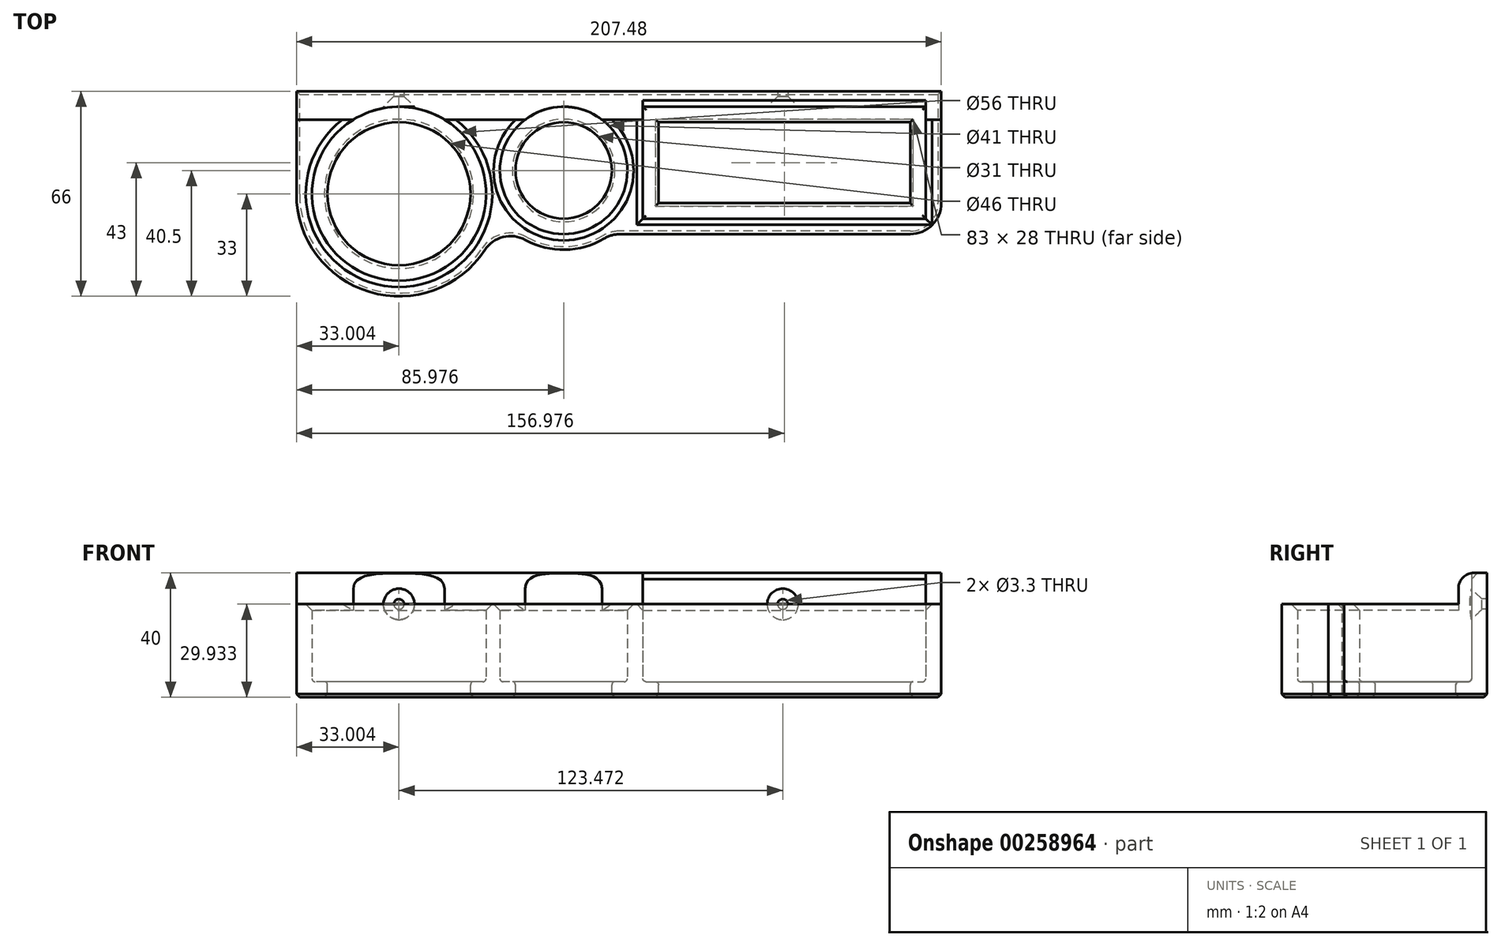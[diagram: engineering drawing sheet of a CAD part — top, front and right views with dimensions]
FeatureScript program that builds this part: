
annotation { "Feature Type Name" : "Feature", "Feature Type Description" : "" }
export const myFeature = defineFeature(function(context is Context, id is Id, definition is map)
    precondition{}
    {
        {
            var Q0;
            Q0=qCreatedBy(makeId("Top.planeOp"),FACE);
            var sketch = newSketch(context, id + "F0", { "sketchPlane" : qUnion([Q0])});
            skCircle(sketch, "E0", {"center": v(-34.24, -28) * mm, "radius": 28 * mm});
            skCircle(sketch, "E1", {"center": v(18.74, -20.5) * mm, "radius": 20.5 * mm});
            skLineSegment(sketch, "E2.bottom", {"start": v(44.24, 0) * mm, "end": v(135.24, 0) * mm});
            skLineSegment(sketch, "E2.top", {"start": v(44.24, -36) * mm, "end": v(135.24, -36) * mm});
            skLineSegment(sketch, "E2.left", {"start": v(44.24, 0) * mm, "end": v(44.24, -36) * mm});
            skLineSegment(sketch, "E2.right", {"start": v(135.24, 0) * mm, "end": v(135.24, -36) * mm});
            skCircle(sketch, "E3.0", {"center": v(-34.24, -28) * mm, "radius": 33 * mm, "construction": true});
            skCircle(sketch, "E4.0", {"center": v(18.74, -20.5) * mm, "radius": 25.5 * mm, "construction": true});
            skLineSegment(sketch, "E5", {"start": v(-67.24, -28) * mm, "end": v(-67.24, 5) * mm});
            skLineSegment(sketch, "E6", {"start": v(-67.24, 5) * mm, "end": v(140.24, 5) * mm});
            skLineSegment(sketch, "E7", {"start": v(140.24, 5) * mm, "end": v(140.24, -41) * mm});
            skLineSegment(sketch, "E8", {"start": v(140.24, -41) * mm, "end": v(33.9, -41) * mm});
            skArc(sketch, "E9", {"start": v(-67.24, -28) * mm, "mid": v(-37.9, -60.8) * mm, "end": v(-2.05, -35.27) * mm});
            skArc(sketch, "E10", {"start": v(-2.05, -35.27) * mm, "mid": v(14.73, -45.68) * mm, "end": v(33.9, -41) * mm});
            skSolve(sketch);
        }
        {
            var Q0;
            Q0=makeQuery(id+"F0.imprint","IMPRINT",FACE,{"disambiguationData":[TD([[makeQuery(id+"F0.imprint","IMPRINT",EDGE,{"derivedFrom":sQuery(id+"F0.wireOp",EDGE,"E0")}),-1.0]])]});
            extrude(context, id + "F1", {"entities" : qUnion([Q0]), "depth" : 30 * mm});
        }
        {
            var Q0;
            Q0=makeQuery(id+"F0.imprint","IMPRINT",FACE,{"disambiguationData":[TD([[makeQuery(id+"F0.imprint","IMPRINT",EDGE,{"derivedFrom":sQuery(id+"F0.wireOp",EDGE,"E0")}),1.0]])]});
            var Q1;
            Q1=makeQuery(id+"F0.imprint","IMPRINT",FACE,{"disambiguationData":[TD([[makeQuery(id+"F0.imprint","IMPRINT",EDGE,{"derivedFrom":sQuery(id+"F0.wireOp",EDGE,"E1")}),1.0]])]});
            var Q2;
            Q2=makeQuery(id+"F0.imprint","IMPRINT",FACE,{"disambiguationData":[TD([[makeQuery(id+"F0.imprint","IMPRINT",EDGE,{"derivedFrom":sQuery(id+"F0.wireOp",EDGE,"E2.bottom")}),-1.0]])]});
            extrude(context, id + "F2", {"entities" : qUnion([Q0, Q1, Q2]), "operationType" : NewBodyOperationType.ADD, "depth" : 5 * mm});
        }
        {
            var Q0;
            Q0=makeQuery(id+"F1.opExtrude","CAP_FACE",FACE,{"disambiguationData":[OSD([sQuery(id+"F0.wireOp",EDGE,"E0"),sQuery(id+"F0.wireOp",EDGE,"E1"),sQuery(id+"F0.wireOp",EDGE,"E2.bottom"),sQuery(id+"F0.wireOp",EDGE,"E2.top"),sQuery(id+"F0.wireOp",EDGE,"E2.left"),sQuery(id+"F0.wireOp",EDGE,"E2.right"),sQuery(id+"F0.wireOp",EDGE,"E5"),sQuery(id+"F0.wireOp",EDGE,"E6"),sQuery(id+"F0.wireOp",EDGE,"E7"),sQuery(id+"F0.wireOp",EDGE,"E8"),sQuery(id+"F0.wireOp",EDGE,"E9"),sQuery(id+"F0.wireOp",EDGE,"E10")])],"isStart":false});
            var sketch = newSketch(context, id + "F3", { "sketchPlane" : qUnion([Q0])});
            skLineSegment(sketch, "E11.bottom", {"start": v(-70.35, 8.83) * mm, "end": v(146.1, 8.83) * mm});
            skLineSegment(sketch, "E11.top", {"start": v(-70.35, -4.18) * mm, "end": v(146.1, -4.18) * mm});
            skLineSegment(sketch, "E11.left", {"start": v(-70.35, 8.83) * mm, "end": v(-70.35, -4.18) * mm});
            skLineSegment(sketch, "E11.right", {"start": v(146.1, 8.83) * mm, "end": v(146.1, -4.18) * mm});
            skSolve(sketch);
        }
        {
            var Q0;
            {var subQ5=makeQuery(id+"F1.opExtrude","CAP_EDGE",EDGE,{"disambiguationData":[OSD([sQuery(id+"F0.wireOp",EDGE,"E2.bottom")])],"isStart":false});Q0=makeQuery(id+"F3.imprint","IMPRINT",FACE,{"disambiguationData":[TD([[makeQuery(id+"F3.imprint","IMPRINT",EDGE,{"derivedFrom":subQ5}),1.0]])]});}
            extrude(context, id + "F4", {"entities" : qUnion([Q0]), "operationType" : NewBodyOperationType.ADD, "depth" : 10 * mm});
        }
        {
            var Q0;
            {var subQ0=sQuery(id+"F3.wireOp",EDGE,"E11.top");Q0=makeQuery(id+"F4.opExtrude","CAP_EDGE",EDGE,{"disambiguationData":[OSD([subQ0]),TDD([makeQuery(id+"F3.imprint","IMPRINT",EDGE,{"disambiguationData":[TD([[makeQuery(id+"F3.imprint","INTERSECT",VERTEX,{"derivedFrom":[makeQuery(id+"F1.opExtrude","CAP_EDGE",EDGE,{"disambiguationData":[OSD([sQuery(id+"F0.wireOp",EDGE,"E5")])],"isStart":false}),subQ0]}),-1.0]])],"derivedFrom":subQ0})])],"isStart":false});}
            var Q1;
            {var subQ0=sQuery(id+"F3.wireOp",EDGE,"E11.top");Q1=makeQuery(id+"F4.opExtrude","CAP_EDGE",EDGE,{"disambiguationData":[OSD([subQ0]),TDD([makeQuery(id+"F3.imprint","IMPRINT",EDGE,{"disambiguationData":[TD([[makeQuery(id+"F3.imprint","INTERSECT",VERTEX,{"disambiguationData":[OD(1.0)],"derivedFrom":[makeQuery(id+"F1.opExtrude","CAP_EDGE",EDGE,{"disambiguationData":[OSD([sQuery(id+"F0.wireOp",EDGE,"E0")])],"isStart":false}),subQ0]}),-1.0]])],"derivedFrom":subQ0})])],"isStart":false});}
            var Q2;
            {var subQ0=sQuery(id+"F3.wireOp",EDGE,"E11.top");Q2=makeQuery(id+"F4.opExtrude","CAP_EDGE",EDGE,{"disambiguationData":[OSD([subQ0]),TDD([makeQuery(id+"F3.imprint","IMPRINT",EDGE,{"disambiguationData":[TD([[makeQuery(id+"F3.imprint","INTERSECT",VERTEX,{"disambiguationData":[OD(1.0)],"derivedFrom":[makeQuery(id+"F1.opExtrude","CAP_EDGE",EDGE,{"disambiguationData":[OSD([sQuery(id+"F0.wireOp",EDGE,"E1")])],"isStart":false}),subQ0]}),-1.0]])],"derivedFrom":subQ0})])],"isStart":false});}
            var Q3;
            {var subQ0=sQuery(id+"F3.wireOp",EDGE,"E11.top");Q3=makeQuery(id+"F4.opExtrude","CAP_EDGE",EDGE,{"disambiguationData":[OSD([subQ0]),TDD([makeQuery(id+"F3.imprint","IMPRINT",EDGE,{"disambiguationData":[TD([[makeQuery(id+"F3.imprint","INTERSECT",VERTEX,{"disambiguationData":[OD(1.0)],"derivedFrom":[makeQuery(id+"F1.opExtrude","CAP_EDGE",EDGE,{"disambiguationData":[OSD([sQuery(id+"F0.wireOp",EDGE,"E1")])],"isStart":false}),subQ0]}),-1.0]])],"derivedFrom":subQ0})])],"isStart":true});}
            var Q4;
            {var subQ0=sQuery(id+"F3.wireOp",EDGE,"E11.top");Q4=makeQuery(id+"F4.opExtrude","CAP_EDGE",EDGE,{"disambiguationData":[OSD([subQ0]),TDD([makeQuery(id+"F3.imprint","IMPRINT",EDGE,{"disambiguationData":[TD([[makeQuery(id+"F3.imprint","INTERSECT",VERTEX,{"disambiguationData":[OD(1.0)],"derivedFrom":[makeQuery(id+"F1.opExtrude","CAP_EDGE",EDGE,{"disambiguationData":[OSD([sQuery(id+"F0.wireOp",EDGE,"E0")])],"isStart":false}),subQ0]}),-1.0]])],"derivedFrom":subQ0})])],"isStart":true});}
            var Q5;
            {var subQ0=sQuery(id+"F3.wireOp",EDGE,"E11.top");Q5=makeQuery(id+"F4.opExtrude","CAP_EDGE",EDGE,{"disambiguationData":[OSD([subQ0]),TDD([makeQuery(id+"F3.imprint","IMPRINT",EDGE,{"disambiguationData":[TD([[makeQuery(id+"F3.imprint","INTERSECT",VERTEX,{"derivedFrom":[makeQuery(id+"F1.opExtrude","CAP_EDGE",EDGE,{"disambiguationData":[OSD([sQuery(id+"F0.wireOp",EDGE,"E5")])],"isStart":false}),subQ0]}),-1.0]])],"derivedFrom":subQ0})])],"isStart":true});}
            var Q6;
            {var subQ0=sQuery(id+"F3.wireOp",EDGE,"E11.top");Q6=makeQuery(id+"F4.opExtrude","CAP_EDGE",EDGE,{"disambiguationData":[OSD([subQ0]),TDD([makeQuery(id+"F3.imprint","IMPRINT",EDGE,{"disambiguationData":[TD([[makeQuery(id+"F3.imprint","INTERSECT",VERTEX,{"derivedFrom":[makeQuery(id+"F1.opExtrude","CAP_EDGE",EDGE,{"disambiguationData":[OSD([sQuery(id+"F0.wireOp",EDGE,"E7")])],"isStart":false}),subQ0]}),1.0]])],"derivedFrom":subQ0})])],"isStart":true});}
            var Q7;
            {var subQ0=sQuery(id+"F3.wireOp",EDGE,"E11.top");Q7=makeQuery(id+"F4.opExtrude","CAP_EDGE",EDGE,{"disambiguationData":[OSD([subQ0]),TDD([makeQuery(id+"F3.imprint","IMPRINT",EDGE,{"disambiguationData":[TD([[makeQuery(id+"F3.imprint","INTERSECT",VERTEX,{"derivedFrom":[makeQuery(id+"F1.opExtrude","CAP_EDGE",EDGE,{"disambiguationData":[OSD([sQuery(id+"F0.wireOp",EDGE,"E7")])],"isStart":false}),subQ0]}),1.0]])],"derivedFrom":subQ0})])],"isStart":false});}
            fillet(context, id + "F5", {"entities" : qUnion([Q0, Q1, Q2, Q3, Q4, Q5, Q6, Q7]), "radius" : 5 * mm, "tangentPropagation" : true, "allowEdgeOverflow" : false});
        }
        {
            var Q0;
            Q0=qCreatedBy(makeId("Front.planeOp"),FACE);
            cPlane(context, id + "F6", {"entities" : qUnion([Q0]), "cplaneType" : CPlaneType.OFFSET, "offset" : 1 * mm, "width" : 150 * mm, "height" : 150 * mm});
        }
        {
            var Q0;
            Q0=qCreatedBy(id+"F6.planeOp",FACE);
            var sketch = newSketch(context, id + "F7", { "sketchPlane" : qUnion([Q0])});
            skPoint(sketch, "E12", {"position": v(-34.24, 29.93) * mm});
            skPoint(sketch, "E13", {"position": v(89.24, 29.93) * mm});
            skSolve(sketch);
        }
        {
            var Q0;
            Q0=sQuery(id+"F7.wireOp",VERTEX,"E13");
            var Q1;
            Q1=sQuery(id+"F7.wireOp",VERTEX,"E12");
            var Q2;
            Q2=makeQuery(id+"F1.opExtrude","SWEPT_BODY",BODY,{"disambiguationData":[OSD([sQuery(id+"F0.wireOp",EDGE,"E0"),sQuery(id+"F0.wireOp",EDGE,"E1"),sQuery(id+"F0.wireOp",EDGE,"E2.bottom"),sQuery(id+"F0.wireOp",EDGE,"E2.top"),sQuery(id+"F0.wireOp",EDGE,"E2.left"),sQuery(id+"F0.wireOp",EDGE,"E2.right"),sQuery(id+"F0.wireOp",EDGE,"E5"),sQuery(id+"F0.wireOp",EDGE,"E6"),sQuery(id+"F0.wireOp",EDGE,"E7"),sQuery(id+"F0.wireOp",EDGE,"E8"),sQuery(id+"F0.wireOp",EDGE,"E9"),sQuery(id+"F0.wireOp",EDGE,"E10")])]});
            hole(context, id + "F8", {"style" : HoleStyle.C_SINK, "endStyle" : HoleEndStyle.BLIND, "holeDiameter" : 3.3 * mm, "cSinkDiameter" : 10 * mm, "cSinkAngle" : 90 * degree, "holeDepth" : 10 * mm, "tappedDepth" : 7 * mm, "tapClearance" : 0, "locations" : qUnion([Q0, Q1]), "scope" : qUnion([Q2])});
        }
        {
            var Q0;
            Q0=makeQuery(id+"F1.opExtrude","SWEPT_EDGE",EDGE,{"disambiguationData":[OSD([sQuery(id+"F0.wireOp",EDGE,"E9"),sQuery(id+"F0.wireOp",EDGE,"E10")])]});
            var Q1;
            Q1=makeQuery(id+"F1.opExtrude","SWEPT_EDGE",EDGE,{"disambiguationData":[OSD([sQuery(id+"F0.wireOp",EDGE,"E8"),sQuery(id+"F0.wireOp",EDGE,"E10")])]});
            var Q2;
            Q2=makeQuery(id+"F1.opExtrude","SWEPT_EDGE",EDGE,{"disambiguationData":[OSD([sQuery(id+"F0.wireOp",EDGE,"E7"),sQuery(id+"F0.wireOp",EDGE,"E8")])]});
            fillet(context, id + "F9", {"entities" : qUnion([Q0, Q1, Q2]), "radius" : 10 * mm, "tangentPropagation" : true, "allowEdgeOverflow" : false});
        }
        {
            var Q0;
            Q0=makeQuery(id+"F1.opExtrude","CAP_EDGE",EDGE,{"disambiguationData":[OSD([sQuery(id+"F0.wireOp",EDGE,"E0")])],"isStart":false});
            var Q1;
            Q1=makeQuery(id+"F1.opExtrude","CAP_EDGE",EDGE,{"disambiguationData":[OSD([sQuery(id+"F0.wireOp",EDGE,"E1")])],"isStart":false});
            var Q2;
            Q2=makeQuery(id+"F1.opExtrude","CAP_EDGE",EDGE,{"disambiguationData":[OSD([sQuery(id+"F0.wireOp",EDGE,"E2.left")])],"isStart":false});
            var Q3;
            Q3=makeQuery(id+"F1.opExtrude","CAP_EDGE",EDGE,{"disambiguationData":[OSD([sQuery(id+"F0.wireOp",EDGE,"E2.top")])],"isStart":false});
            var Q4;
            Q4=makeQuery(id+"F1.opExtrude","CAP_EDGE",EDGE,{"disambiguationData":[OSD([sQuery(id+"F0.wireOp",EDGE,"E2.right")])],"isStart":false});
            var Q5;
            {var subQ0=sQuery(id+"F0.wireOp",EDGE,"E2.bottom");var subQ1=sQuery(id+"F3.wireOp",EDGE,"E11.top");Q5=makeQuery(id+"F5.opFillet","BLEND_EDGE",EDGE,{"blendedFrom":[makeQuery(id+"F4.opExtrude","CAP_EDGE",EDGE,{"disambiguationData":[OSD([subQ1]),TDD([makeQuery(id+"F3.imprint","IMPRINT",EDGE,{"disambiguationData":[TD([[makeQuery(id+"F3.imprint","INTERSECT",VERTEX,{"derivedFrom":[makeQuery(id+"F1.opExtrude","CAP_EDGE",EDGE,{"disambiguationData":[OSD([sQuery(id+"F0.wireOp",EDGE,"E5")])],"isStart":false}),subQ1]}),-1.0]])],"derivedFrom":subQ1})])],"isStart":false}),makeQuery(id+"F4.boolean.opBoolean","MERGE",FACE,{"derivedFrom":[makeQuery(id+"F1.opExtrude","SWEPT_FACE",FACE,{"disambiguationData":[OSD([subQ0])]}),makeQuery(id+"F4.opExtrude","SWEPT_FACE",FACE,{"disambiguationData":[OSD([subQ0])]})]})],"blendedInto":[makeQuery(id+"F4.boolean.opBoolean","MERGE",FACE,{"derivedFrom":[makeQuery(id+"F1.opExtrude","SWEPT_FACE",FACE,{"disambiguationData":[OSD([subQ0])]}),makeQuery(id+"F4.opExtrude","SWEPT_FACE",FACE,{"disambiguationData":[OSD([subQ0])]})]})]});}
            chamfer(context, id + "F10", {"entities" : qUnion([Q0, Q1, Q2, Q3, Q4, Q5]), "width" : 2 * mm, "tangentPropagation" : true});
        }
        {
            var Q0;
            Q0=makeQuery(id+"F2.opExtrude","CAP_FACE",FACE,{"disambiguationData":[OSD([sQuery(id+"F0.wireOp",EDGE,"E0")])],"isStart":false});
            var sketch = newSketch(context, id + "F11", { "sketchPlane" : qUnion([Q0])});
            skCircle(sketch, "E14", {"center": v(-34.24, -28) * mm, "radius": 23 * mm});
            skCircle(sketch, "E15", {"center": v(18.74, -20.5) * mm, "radius": 15.5 * mm});
            skLineSegment(sketch, "E16.0", {"start": v(49.24, -5) * mm, "end": v(49.24, -31) * mm});
            skLineSegment(sketch, "E16.1", {"start": v(49.24, -5) * mm, "end": v(130.24, -5) * mm});
            skLineSegment(sketch, "E16.2", {"start": v(130.24, -5) * mm, "end": v(130.24, -31) * mm});
            skLineSegment(sketch, "E16.3", {"start": v(49.24, -31) * mm, "end": v(130.24, -31) * mm});
            skSolve(sketch);
        }
        {
            var Q0;
            Q0=makeQuery(id+"F11.imprint","IMPRINT",FACE,{"disambiguationData":[TD([[makeQuery(id+"F11.imprint","IMPRINT",EDGE,{"derivedFrom":sQuery(id+"F11.wireOp",EDGE,"E14")}),1.0]])]});
            var Q1;
            Q1=makeQuery(id+"F11.imprint","IMPRINT",FACE,{"disambiguationData":[TD([[makeQuery(id+"F11.imprint","IMPRINT",EDGE,{"derivedFrom":sQuery(id+"F11.wireOp",EDGE,"E15")}),1.0]])]});
            var Q2;
            Q2=makeQuery(id+"F11.imprint","IMPRINT",FACE,{"disambiguationData":[TD([[makeQuery(id+"F11.imprint","IMPRINT",EDGE,{"derivedFrom":sQuery(id+"F11.wireOp",EDGE,"E16.0")}),1.0]])]});
            extrude(context, id + "F12", {"entities" : qUnion([Q0, Q1, Q2]), "operationType" : NewBodyOperationType.REMOVE, "oppositeDirection" : true, "depth" : 25 * mm});
        }
        {
            var Q0;
            {var subQ0=sQuery(id+"F0.wireOp",EDGE,"E2.right");var subQ1=sQuery(id+"F0.wireOp",EDGE,"E2.left");var subQ2=sQuery(id+"F0.wireOp",EDGE,"E2.top");var subQ3=sQuery(id+"F0.wireOp",EDGE,"E2.bottom");var subQ4=sQuery(id+"F0.wireOp",EDGE,"E1");var subQ5=sQuery(id+"F0.wireOp",EDGE,"E0");Q0=makeQuery(id+"F2.boolean.opBoolean","MERGE",FACE,{"derivedFrom":[makeQuery(id+"F1.opExtrude","CAP_FACE",FACE,{"disambiguationData":[OSD([subQ5,subQ4,subQ3,subQ2,subQ1,subQ0,sQuery(id+"F0.wireOp",EDGE,"E5"),sQuery(id+"F0.wireOp",EDGE,"E6"),sQuery(id+"F0.wireOp",EDGE,"E7"),sQuery(id+"F0.wireOp",EDGE,"E8"),sQuery(id+"F0.wireOp",EDGE,"E9"),sQuery(id+"F0.wireOp",EDGE,"E10")])],"isStart":true}),makeQuery(id+"F2.opExtrude","CAP_FACE",FACE,{"disambiguationData":[OSD([subQ5])],"isStart":true}),makeQuery(id+"F2.opExtrude","CAP_FACE",FACE,{"disambiguationData":[OSD([subQ4])],"isStart":true}),makeQuery(id+"F2.opExtrude","CAP_FACE",FACE,{"disambiguationData":[OSD([subQ3,subQ2,subQ1,subQ0])],"isStart":true})]});}
            chamfer(context, id + "F13", {"entities" : qUnion([Q0]), "width" : 1 * mm, "tangentPropagation" : true});
        }
        {
            var Q0;
            Q0=makeQuery(id+"F2.opExtrude","CAP_FACE",FACE,{"disambiguationData":[OSD([sQuery(id+"F0.wireOp",EDGE,"E0")])],"isStart":false});
            var Q1;
            Q1=makeQuery(id+"F2.opExtrude","CAP_FACE",FACE,{"disambiguationData":[OSD([sQuery(id+"F0.wireOp",EDGE,"E1")])],"isStart":false});
            var Q2;
            Q2=makeQuery(id+"F2.opExtrude","CAP_FACE",FACE,{"disambiguationData":[OSD([sQuery(id+"F0.wireOp",EDGE,"E2.bottom"),sQuery(id+"F0.wireOp",EDGE,"E2.top"),sQuery(id+"F0.wireOp",EDGE,"E2.left"),sQuery(id+"F0.wireOp",EDGE,"E2.right")])],"isStart":false});
            fillet(context, id + "F14", {"entities" : qUnion([Q0, Q1, Q2]), "radius" : 1 * mm, "tangentPropagation" : true, "allowEdgeOverflow" : false});
        }
    });
